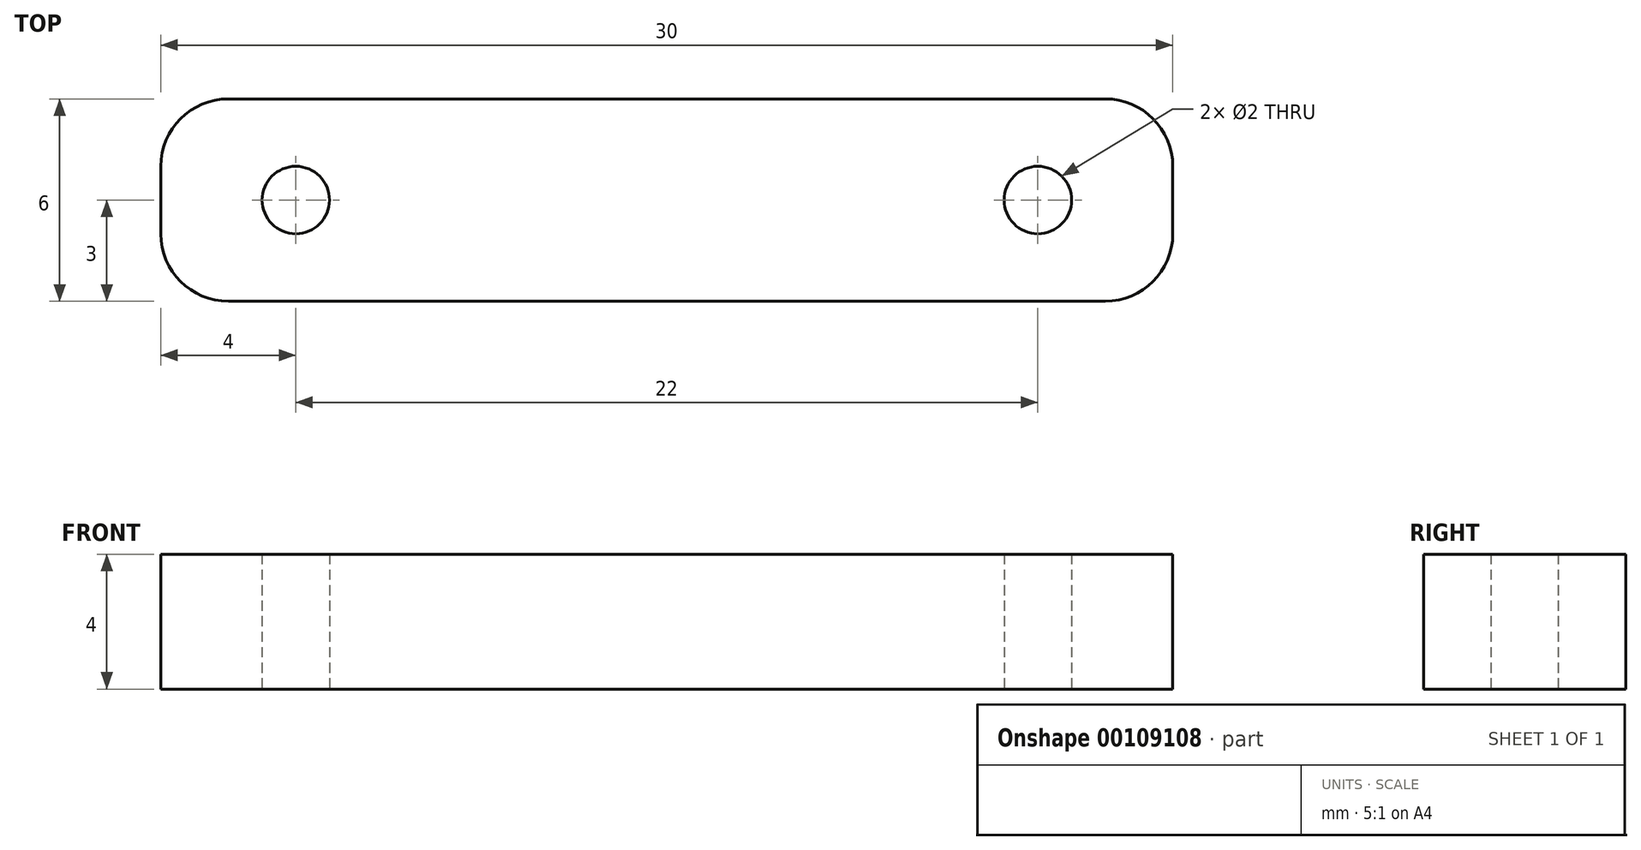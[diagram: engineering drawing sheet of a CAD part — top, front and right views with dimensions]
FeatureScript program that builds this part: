
annotation { "Feature Type Name" : "Feature", "Feature Type Description" : "" }
export const myFeature = defineFeature(function(context is Context, id is Id, definition is map)
    precondition{}
    {
        {
            var Q0;
            Q0=qCreatedBy(makeId("Top.planeOp"),FACE);
            var sketch = newSketch(context, id + "F0", { "sketchPlane" : qUnion([Q0])});
            skLineSegment(sketch, "E0.bottom", {"start": v(-15, 3) * mm, "end": v(15, 3) * mm});
            skLineSegment(sketch, "E0.top", {"start": v(-15, -3) * mm, "end": v(15, -3) * mm});
            skLineSegment(sketch, "E0.left", {"start": v(-15, 3) * mm, "end": v(-15, -3) * mm});
            skLineSegment(sketch, "E0.right", {"start": v(15, 3) * mm, "end": v(15, -3) * mm});
            skPoint(sketch, "E0.middle", {"position": v(0, 0) * mm});
            skCircle(sketch, "E1", {"center": v(-11, 0) * mm, "radius": 1 * mm});
            skCircle(sketch, "E2", {"center": v(11, 0) * mm, "radius": 1 * mm});
            skSolve(sketch);
        }
        {
            var Q0;
            Q0=makeQuery(id+"F0.imprint","IMPRINT",FACE,{"disambiguationData":[TD([[makeQuery(id+"F0.imprint","IMPRINT",EDGE,{"derivedFrom":sQuery(id+"F0.wireOp",EDGE,"E0.bottom")}),-1.0]])]});
            extrude(context, id + "F1", {"entities" : qUnion([Q0]), "depth" : 4 * mm});
        }
        {
            var Q0;
            Q0=makeQuery(id+"F1.opExtrude","SWEPT_EDGE",EDGE,{"disambiguationData":[OSD([sQuery(id+"F0.wireOp",EDGE,"E0.bottom"),sQuery(id+"F0.wireOp",EDGE,"E0.left")])]});
            var Q1;
            Q1=makeQuery(id+"F1.opExtrude","SWEPT_EDGE",EDGE,{"disambiguationData":[OSD([sQuery(id+"F0.wireOp",EDGE,"E0.top"),sQuery(id+"F0.wireOp",EDGE,"E0.left")])]});
            var Q2;
            Q2=makeQuery(id+"F1.opExtrude","SWEPT_EDGE",EDGE,{"disambiguationData":[OSD([sQuery(id+"F0.wireOp",EDGE,"E0.bottom"),sQuery(id+"F0.wireOp",EDGE,"E0.right")])]});
            var Q3;
            Q3=makeQuery(id+"F1.opExtrude","SWEPT_EDGE",EDGE,{"disambiguationData":[OSD([sQuery(id+"F0.wireOp",EDGE,"E0.top"),sQuery(id+"F0.wireOp",EDGE,"E0.right")])]});
            fillet(context, id + "F2", {"entities" : qUnion([Q0, Q1, Q2, Q3]), "radius" : 2 * mm, "tangentPropagation" : true, "allowEdgeOverflow" : false});
        }
    });
